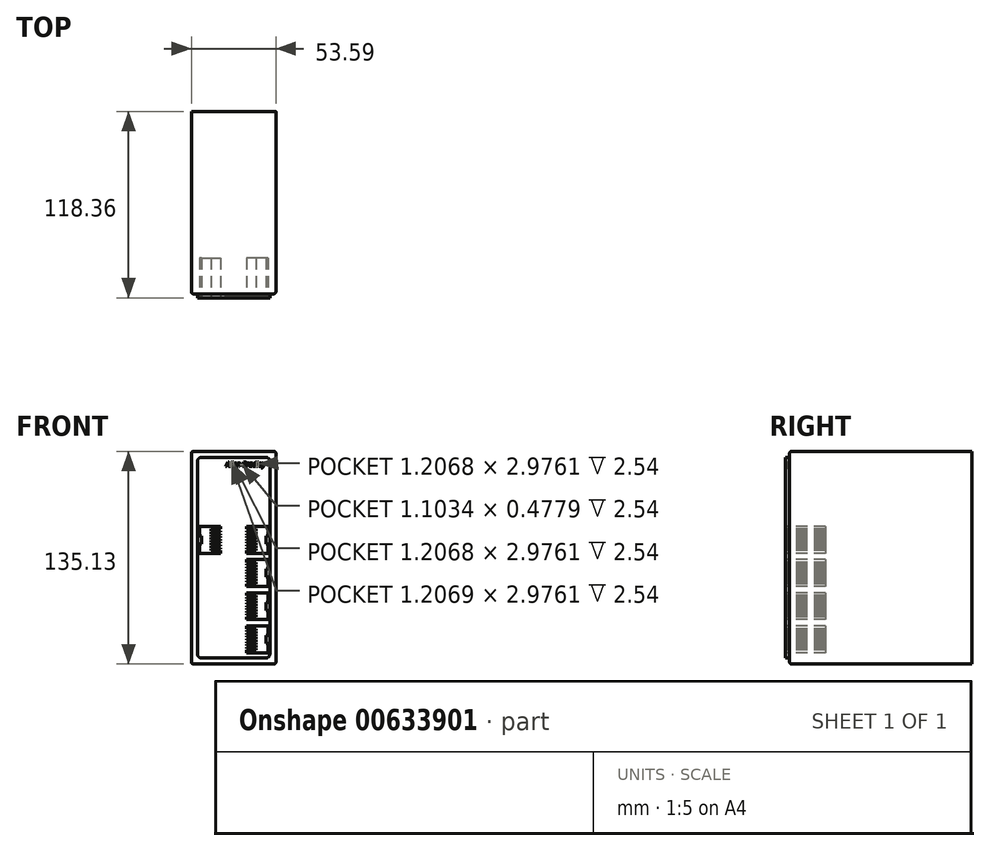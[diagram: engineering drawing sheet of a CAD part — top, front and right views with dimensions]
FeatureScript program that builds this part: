
annotation { "Feature Type Name" : "Feature", "Feature Type Description" : "" }
export const myFeature = defineFeature(function(context is Context, id is Id, definition is map)
    precondition{}
    {
        {
            var Q0;
            Q0=qCreatedBy(makeId("Front.planeOp"),FACE);
            var sketch = newSketch(context, id + "F0", { "sketchPlane" : qUnion([Q0])});
            skLineSegment(sketch, "E0.bottom", {"start": v(0, 0) * mm, "end": v(53.6, 0) * mm});
            skLineSegment(sketch, "E0.top", {"start": v(0, 135.13) * mm, "end": v(53.6, 135.13) * mm});
            skLineSegment(sketch, "E0.left", {"start": v(0, 0) * mm, "end": v(0, 135.13) * mm});
            skLineSegment(sketch, "E0.right", {"start": v(53.6, 0) * mm, "end": v(53.6, 135.13) * mm});
            skSolve(sketch);
        }
        {
            var Q0;
            Q0=makeQuery(id+"F0.imprint","IMPRINT",FACE,{"disambiguationData":[TD([[makeQuery(id+"F0.imprint","IMPRINT",EDGE,{"derivedFrom":sQuery(id+"F0.wireOp",EDGE,"E0.bottom")}),1.0]])]});
            extrude(context, id + "F1", {"entities" : qUnion([Q0]), "depth" : 115.82 * mm, "offsetDistance" : 25.4 * mm});
        }
        {
            var Q0;
            Q0=makeQuery(id+"F1.opExtrude","CAP_FACE",FACE,{"disambiguationData":[OSD([sQuery(id+"F0.wireOp",EDGE,"E0.bottom"),sQuery(id+"F0.wireOp",EDGE,"E0.top"),sQuery(id+"F0.wireOp",EDGE,"E0.left"),sQuery(id+"F0.wireOp",EDGE,"E0.right")])],"isStart":false});
            var sketch = newSketch(context, id + "F2", { "sketchPlane" : qUnion([Q0])});
            skLineSegment(sketch, "E1.0", {"start": v(6.35, 131.32) * mm, "end": v(47.24, 131.32) * mm});
            skLineSegment(sketch, "E1.1", {"start": v(3.81, 6.35) * mm, "end": v(3.81, 128.78) * mm});
            skLineSegment(sketch, "E1.2", {"start": v(6.35, 3.81) * mm, "end": v(47.24, 3.81) * mm});
            skLineSegment(sketch, "E1.3", {"start": v(49.78, 6.35) * mm, "end": v(49.78, 128.78) * mm});
            skPoint(sketch, "E2.visualSharp", {"position": v(3.81, 131.32) * mm});
            skArc(sketch, "E2.filletArc", {"start": v(6.35, 131.32) * mm, "mid": v(4.55, 130.57) * mm, "end": v(3.81, 128.78) * mm});
            skPoint(sketch, "E3.visualSharp", {"position": v(49.78, 131.32) * mm});
            skArc(sketch, "E3.filletArc", {"start": v(49.78, 128.78) * mm, "mid": v(49.04, 130.57) * mm, "end": v(47.24, 131.32) * mm});
            skPoint(sketch, "E4.visualSharp", {"position": v(49.78, 3.81) * mm});
            skArc(sketch, "E4.filletArc", {"start": v(47.24, 3.81) * mm, "mid": v(49.04, 4.55) * mm, "end": v(49.78, 6.35) * mm});
            skPoint(sketch, "E5.visualSharp", {"position": v(3.81, 3.81) * mm});
            skArc(sketch, "E5.filletArc", {"start": v(3.81, 6.35) * mm, "mid": v(4.55, 4.55) * mm, "end": v(6.35, 3.81) * mm});
            skText(sketch, "E6", { "text": "Allen-Bradley", "fontName": "OpenSans-BoldItalic.ttf"});
            const initialGuessF2  = {"E6": [0.02189, 0.12554, 1, 0, 0.00282]};
            skSetInitialGuess(sketch, initialGuessF2);
            skSolve(sketch);
        }
        {
            var Q0;
            Q0 = qSketchRegion(id + "F2", true);
            extrude(context, id + "F3", {"entities" : qUnion([Q0]), "operationType" : NewBodyOperationType.ADD, "depth" : 2.54 * mm, "offsetDistance" : 25.4 * mm});
        }
        {
            var Q0;
            Q0=makeQuery(id+"F1.opExtrude","SWEPT_EDGE",EDGE,{"disambiguationData":[OSD([sQuery(id+"F0.wireOp",EDGE,"E0.top"),sQuery(id+"F0.wireOp",EDGE,"E0.right")])]});
            var Q1;
            Q1=makeQuery(id+"F1.opExtrude","SWEPT_EDGE",EDGE,{"disambiguationData":[OSD([sQuery(id+"F0.wireOp",EDGE,"E0.top"),sQuery(id+"F0.wireOp",EDGE,"E0.left")])]});
            var Q2;
            Q2=makeQuery(id+"F1.opExtrude","CAP_EDGE",EDGE,{"disambiguationData":[OSD([sQuery(id+"F0.wireOp",EDGE,"E0.right")])],"isStart":false});
            var Q3;
            Q3=makeQuery(id+"F1.opExtrude","SWEPT_EDGE",EDGE,{"disambiguationData":[OSD([sQuery(id+"F0.wireOp",EDGE,"E0.bottom"),sQuery(id+"F0.wireOp",EDGE,"E0.right")])]});
            var Q4;
            Q4=makeQuery(id+"F1.opExtrude","CAP_EDGE",EDGE,{"disambiguationData":[OSD([sQuery(id+"F0.wireOp",EDGE,"E0.left")])],"isStart":false});
            var Q5;
            Q5=makeQuery(id+"F1.opExtrude","CAP_EDGE",EDGE,{"disambiguationData":[OSD([sQuery(id+"F0.wireOp",EDGE,"E0.top")])],"isStart":false});
            var Q6;
            Q6=makeQuery(id+"F1.opExtrude","CAP_EDGE",EDGE,{"disambiguationData":[OSD([sQuery(id+"F0.wireOp",EDGE,"E0.bottom")])],"isStart":false});
            var Q7;
            Q7=makeQuery(id+"F1.opExtrude","SWEPT_EDGE",EDGE,{"disambiguationData":[OSD([sQuery(id+"F0.wireOp",EDGE,"E0.bottom"),sQuery(id+"F0.wireOp",EDGE,"E0.left")])]});
            fillet(context, id + "F4", {"entities" : qUnion([Q0, Q1, Q2, Q3, Q4, Q5, Q6, Q7]), "radius" : 1.27 * mm, "tangentPropagation" : true, "allowEdgeOverflow" : false});
        }
        {
            var Q0;
            Q0=makeQuery(id+"F3.opExtrude","CAP_FACE",FACE,{"disambiguationData":[OSD([sQuery(id+"F2.wireOp",EDGE,"E1.0"),sQuery(id+"F2.wireOp",EDGE,"E1.1"),sQuery(id+"F2.wireOp",EDGE,"E1.2"),sQuery(id+"F2.wireOp",EDGE,"E1.3"),sQuery(id+"F2.wireOp",EDGE,"E2.filletArc"),sQuery(id+"F2.wireOp",EDGE,"E3.filletArc"),sQuery(id+"F2.wireOp",EDGE,"E4.filletArc"),sQuery(id+"F2.wireOp",EDGE,"E5.filletArc"),sQuery(id+"F2.wireOp",EDGE,"E6.sketch_text.stroke-0"),sQuery(id+"F2.wireOp",EDGE,"E6.sketch_text.stroke-1"),sQuery(id+"F2.wireOp",EDGE,"E6.sketch_text.stroke-2"),sQuery(id+"F2.wireOp",EDGE,"E6.sketch_text.stroke-3"),sQuery(id+"F2.wireOp",EDGE,"E6.sketch_text.stroke-4"),sQuery(id+"F2.wireOp",EDGE,"E6.sketch_text.stroke-5"),sQuery(id+"F2.wireOp",EDGE,"E6.sketch_text.stroke-6"),sQuery(id+"F2.wireOp",EDGE,"E6.sketch_text.stroke-7"),sQuery(id+"F2.wireOp",EDGE,"E6.sketch_text.stroke-14"),sQuery(id+"F2.wireOp",EDGE,"E6.sketch_text.stroke-15"),sQuery(id+"F2.wireOp",EDGE,"E6.sketch_text.stroke-16"),sQuery(id+"F2.wireOp",EDGE,"E6.sketch_text.stroke-17"),sQuery(id+"F2.wireOp",EDGE,"E6.sketch_text.stroke-18"),sQuery(id+"F2.wireOp",EDGE,"E6.sketch_text.stroke-19"),sQuery(id+"F2.wireOp",EDGE,"E6.sketch_text.stroke-20"),sQuery(id+"F2.wireOp",EDGE,"E6.sketch_text.stroke-21"),sQuery(id+"F2.wireOp",EDGE,"E6.sketch_text.stroke-28"),sQuery(id+"F2.wireOp",EDGE,"E6.sketch_text.stroke-29"),sQuery(id+"F2.wireOp",EDGE,"E6.sketch_text.stroke-30"),sQuery(id+"F2.wireOp",EDGE,"E6.sketch_text.stroke-31"),sQuery(id+"F2.wireOp",EDGE,"E6.sketch_text.stroke-32"),sQuery(id+"F2.wireOp",EDGE,"E6.sketch_text.stroke-33"),sQuery(id+"F2.wireOp",EDGE,"E6.sketch_text.stroke-34"),sQuery(id+"F2.wireOp",EDGE,"E6.sketch_text.stroke-35"),sQuery(id+"F2.wireOp",EDGE,"E6.sketch_text.stroke-36"),sQuery(id+"F2.wireOp",EDGE,"E6.sketch_text.stroke-37"),sQuery(id+"F2.wireOp",EDGE,"E6.sketch_text.stroke-38"),sQuery(id+"F2.wireOp",EDGE,"E6.sketch_text.stroke-39"),sQuery(id+"F2.wireOp",EDGE,"E6.sketch_text.stroke-40"),sQuery(id+"F2.wireOp",EDGE,"E6.sketch_text.stroke-41"),sQuery(id+"F2.wireOp",EDGE,"E6.sketch_text.stroke-42"),sQuery(id+"F2.wireOp",EDGE,"E6.sketch_text.stroke-43"),sQuery(id+"F2.wireOp",EDGE,"E6.sketch_text.stroke-44"),sQuery(id+"F2.wireOp",EDGE,"E6.sketch_text.stroke-45"),sQuery(id+"F2.wireOp",EDGE,"E6.sketch_text.stroke-46"),sQuery(id+"F2.wireOp",EDGE,"E6.sketch_text.stroke-47"),sQuery(id+"F2.wireOp",EDGE,"E6.sketch_text.stroke-48"),sQuery(id+"F2.wireOp",EDGE,"E6.sketch_text.stroke-49"),sQuery(id+"F2.wireOp",EDGE,"E6.sketch_text.stroke-50"),sQuery(id+"F2.wireOp",EDGE,"E6.sketch_text.stroke-51"),sQuery(id+"F2.wireOp",EDGE,"E6.sketch_text.stroke-52"),sQuery(id+"F2.wireOp",EDGE,"E6.sketch_text.stroke-53"),sQuery(id+"F2.wireOp",EDGE,"E6.sketch_text.stroke-54"),sQuery(id+"F2.wireOp",EDGE,"E6.sketch_text.stroke-55"),sQuery(id+"F2.wireOp",EDGE,"E6.sketch_text.stroke-56"),sQuery(id+"F2.wireOp",EDGE,"E6.sketch_text.stroke-57"),sQuery(id+"F2.wireOp",EDGE,"E6.sketch_text.stroke-58"),sQuery(id+"F2.wireOp",EDGE,"E6.sketch_text.stroke-59"),sQuery(id+"F2.wireOp",EDGE,"E6.sketch_text.stroke-60"),sQuery(id+"F2.wireOp",EDGE,"E6.sketch_text.stroke-61"),sQuery(id+"F2.wireOp",EDGE,"E6.sketch_text.stroke-62"),sQuery(id+"F2.wireOp",EDGE,"E6.sketch_text.stroke-63"),sQuery(id+"F2.wireOp",EDGE,"E6.sketch_text.stroke-64"),sQuery(id+"F2.wireOp",EDGE,"E6.sketch_text.stroke-65"),sQuery(id+"F2.wireOp",EDGE,"E6.sketch_text.stroke-66"),sQuery(id+"F2.wireOp",EDGE,"E6.sketch_text.stroke-67"),sQuery(id+"F2.wireOp",EDGE,"E6.sketch_text.stroke-68"),sQuery(id+"F2.wireOp",EDGE,"E6.sketch_text.stroke-69"),sQuery(id+"F2.wireOp",EDGE,"E6.sketch_text.stroke-70"),sQuery(id+"F2.wireOp",EDGE,"E6.sketch_text.stroke-71"),sQuery(id+"F2.wireOp",EDGE,"E6.sketch_text.stroke-72"),sQuery(id+"F2.wireOp",EDGE,"E6.sketch_text.stroke-73"),sQuery(id+"F2.wireOp",EDGE,"E6.sketch_text.stroke-74"),sQuery(id+"F2.wireOp",EDGE,"E6.sketch_text.stroke-75"),sQuery(id+"F2.wireOp",EDGE,"E6.sketch_text.stroke-76"),sQuery(id+"F2.wireOp",EDGE,"E6.sketch_text.stroke-77"),sQuery(id+"F2.wireOp",EDGE,"E6.sketch_text.stroke-78"),sQuery(id+"F2.wireOp",EDGE,"E6.sketch_text.stroke-91"),sQuery(id+"F2.wireOp",EDGE,"E6.sketch_text.stroke-92"),sQuery(id+"F2.wireOp",EDGE,"E6.sketch_text.stroke-93"),sQuery(id+"F2.wireOp",EDGE,"E6.sketch_text.stroke-94"),sQuery(id+"F2.wireOp",EDGE,"E6.sketch_text.stroke-95"),sQuery(id+"F2.wireOp",EDGE,"E6.sketch_text.stroke-96"),sQuery(id+"F2.wireOp",EDGE,"E6.sketch_text.stroke-97"),sQuery(id+"F2.wireOp",EDGE,"E6.sketch_text.stroke-98"),sQuery(id+"F2.wireOp",EDGE,"E6.sketch_text.stroke-99"),sQuery(id+"F2.wireOp",EDGE,"E6.sketch_text.stroke-100"),sQuery(id+"F2.wireOp",EDGE,"E6.sketch_text.stroke-101"),sQuery(id+"F2.wireOp",EDGE,"E6.sketch_text.stroke-102"),sQuery(id+"F2.wireOp",EDGE,"E6.sketch_text.stroke-103"),sQuery(id+"F2.wireOp",EDGE,"E6.sketch_text.stroke-104"),sQuery(id+"F2.wireOp",EDGE,"E6.sketch_text.stroke-105"),sQuery(id+"F2.wireOp",EDGE,"E6.sketch_text.stroke-106"),sQuery(id+"F2.wireOp",EDGE,"E6.sketch_text.stroke-107"),sQuery(id+"F2.wireOp",EDGE,"E6.sketch_text.stroke-108"),sQuery(id+"F2.wireOp",EDGE,"E6.sketch_text.stroke-109"),sQuery(id+"F2.wireOp",EDGE,"E6.sketch_text.stroke-110"),sQuery(id+"F2.wireOp",EDGE,"E6.sketch_text.stroke-111"),sQuery(id+"F2.wireOp",EDGE,"E6.sketch_text.stroke-112"),sQuery(id+"F2.wireOp",EDGE,"E6.sketch_text.stroke-113"),sQuery(id+"F2.wireOp",EDGE,"E6.sketch_text.stroke-114"),sQuery(id+"F2.wireOp",EDGE,"E6.sketch_text.stroke-115"),sQuery(id+"F2.wireOp",EDGE,"E6.sketch_text.stroke-116"),sQuery(id+"F2.wireOp",EDGE,"E6.sketch_text.stroke-117"),sQuery(id+"F2.wireOp",EDGE,"E6.sketch_text.stroke-128"),sQuery(id+"F2.wireOp",EDGE,"E6.sketch_text.stroke-129"),sQuery(id+"F2.wireOp",EDGE,"E6.sketch_text.stroke-130"),sQuery(id+"F2.wireOp",EDGE,"E6.sketch_text.stroke-131"),sQuery(id+"F2.wireOp",EDGE,"E6.sketch_text.stroke-132"),sQuery(id+"F2.wireOp",EDGE,"E6.sketch_text.stroke-133"),sQuery(id+"F2.wireOp",EDGE,"E6.sketch_text.stroke-134"),sQuery(id+"F2.wireOp",EDGE,"E6.sketch_text.stroke-135"),sQuery(id+"F2.wireOp",EDGE,"E6.sketch_text.stroke-136"),sQuery(id+"F2.wireOp",EDGE,"E6.sketch_text.stroke-137"),sQuery(id+"F2.wireOp",EDGE,"E6.sketch_text.stroke-138"),sQuery(id+"F2.wireOp",EDGE,"E6.sketch_text.stroke-139"),sQuery(id+"F2.wireOp",EDGE,"E6.sketch_text.stroke-140"),sQuery(id+"F2.wireOp",EDGE,"E6.sketch_text.stroke-141"),sQuery(id+"F2.wireOp",EDGE,"E6.sketch_text.stroke-142"),sQuery(id+"F2.wireOp",EDGE,"E6.sketch_text.stroke-143"),sQuery(id+"F2.wireOp",EDGE,"E6.sketch_text.stroke-144"),sQuery(id+"F2.wireOp",EDGE,"E6.sketch_text.stroke-145"),sQuery(id+"F2.wireOp",EDGE,"E6.sketch_text.stroke-155"),sQuery(id+"F2.wireOp",EDGE,"E6.sketch_text.stroke-156"),sQuery(id+"F2.wireOp",EDGE,"E6.sketch_text.stroke-157"),sQuery(id+"F2.wireOp",EDGE,"E6.sketch_text.stroke-158"),sQuery(id+"F2.wireOp",EDGE,"E6.sketch_text.stroke-165"),sQuery(id+"F2.wireOp",EDGE,"E6.sketch_text.stroke-166"),sQuery(id+"F2.wireOp",EDGE,"E6.sketch_text.stroke-167"),sQuery(id+"F2.wireOp",EDGE,"E6.sketch_text.stroke-168"),sQuery(id+"F2.wireOp",EDGE,"E6.sketch_text.stroke-169"),sQuery(id+"F2.wireOp",EDGE,"E6.sketch_text.stroke-170"),sQuery(id+"F2.wireOp",EDGE,"E6.sketch_text.stroke-171"),sQuery(id+"F2.wireOp",EDGE,"E6.sketch_text.stroke-172"),sQuery(id+"F2.wireOp",EDGE,"E6.sketch_text.stroke-173"),sQuery(id+"F2.wireOp",EDGE,"E6.sketch_text.stroke-174"),sQuery(id+"F2.wireOp",EDGE,"E6.sketch_text.stroke-175"),sQuery(id+"F2.wireOp",EDGE,"E6.sketch_text.stroke-176"),sQuery(id+"F2.wireOp",EDGE,"E6.sketch_text.stroke-177"),sQuery(id+"F2.wireOp",EDGE,"E6.sketch_text.stroke-178"),sQuery(id+"F2.wireOp",EDGE,"E6.sketch_text.stroke-179"),sQuery(id+"F2.wireOp",EDGE,"E6.sketch_text.stroke-180"),sQuery(id+"F2.wireOp",EDGE,"E6.sketch_text.stroke-181"),sQuery(id+"F2.wireOp",EDGE,"E6.sketch_text.stroke-182"),sQuery(id+"F2.wireOp",EDGE,"E6.sketch_text.stroke-183"),sQuery(id+"F2.wireOp",EDGE,"E6.sketch_text.stroke-184"),sQuery(id+"F2.wireOp",EDGE,"E6.sketch_text.stroke-185"),sQuery(id+"F2.wireOp",EDGE,"E6.sketch_text.stroke-186"),sQuery(id+"F2.wireOp",EDGE,"E6.sketch_text.stroke-187"),sQuery(id+"F2.wireOp",EDGE,"E6.sketch_text.stroke-188"),sQuery(id+"F2.wireOp",EDGE,"E6.sketch_text.stroke-189"),sQuery(id+"F2.wireOp",EDGE,"E6.sketch_text.stroke-190"),sQuery(id+"F2.wireOp",EDGE,"E6.sketch_text.stroke-191"),sQuery(id+"F2.wireOp",EDGE,"E6.sketch_text.stroke-192"),sQuery(id+"F2.wireOp",EDGE,"E6.sketch_text.stroke-193"),sQuery(id+"F2.wireOp",EDGE,"E6.sketch_text.stroke-194"),sQuery(id+"F2.wireOp",EDGE,"E6.sketch_text.stroke-195"),sQuery(id+"F2.wireOp",EDGE,"E6.sketch_text.stroke-196"),sQuery(id+"F2.wireOp",EDGE,"E6.sketch_text.stroke-197"),sQuery(id+"F2.wireOp",EDGE,"E6.sketch_text.stroke-198"),sQuery(id+"F2.wireOp",EDGE,"E6.sketch_text.stroke-199")])],"isStart":false});
            var sketch = newSketch(context, id + "F5", { "sketchPlane" : qUnion([Q0])});
            skLineSegment(sketch, "E7.top", {"start": v(5.08, 70.39) * mm, "end": v(18.55, 70.39) * mm});
            skLineSegment(sketch, "E7.left", {"start": v(5.08, 87.4) * mm, "end": v(5.08, 70.39) * mm});
            skLineSegment(sketch, "E7.right", {"start": v(18.55, 87.4) * mm, "end": v(18.55, 70.39) * mm});
            skLineSegment(sketch, "E8", {"start": v(6.35, 78.9) * mm, "end": v(6.35, 81.44) * mm});
            skLineSegment(sketch, "E9", {"start": v(6.35, 81.44) * mm, "end": v(5.08, 81.44) * mm});
            skLineSegment(sketch, "E10.MirrorCS", {"start": v(6.35, 76.36) * mm, "end": v(5.08, 76.36) * mm});
            skLineSegment(sketch, "E11.MirrorCS", {"start": v(6.35, 78.9) * mm, "end": v(6.35, 76.36) * mm});
            skLineSegment(sketch, "E12.bottom", {"start": v(12.48, 73.23) * mm, "end": v(18.56, 73.23) * mm});
            skLineSegment(sketch, "E12.top", {"start": v(12.48, 72.09) * mm, "end": v(18.56, 72.09) * mm});
            skLineSegment(sketch, "E12.left", {"start": v(12.48, 73.23) * mm, "end": v(12.48, 72.09) * mm});
            skLineSegment(sketch, "E12.right", {"start": v(18.56, 73.23) * mm, "end": v(18.56, 72.09) * mm});
            skLineSegment(sketch, "E13.0.1.0", {"start": v(18.56, 75.01) * mm, "end": v(18.56, 73.86) * mm});
            skLineSegment(sketch, "E13.0.1.1", {"start": v(12.48, 75.01) * mm, "end": v(12.48, 73.86) * mm});
            skLineSegment(sketch, "E13.0.1.2", {"start": v(12.48, 75.01) * mm, "end": v(18.56, 75.01) * mm});
            skLineSegment(sketch, "E13.0.1.3", {"start": v(12.48, 73.86) * mm, "end": v(18.56, 73.86) * mm});
            skLineSegment(sketch, "E13.0.2.0", {"start": v(18.56, 76.79) * mm, "end": v(18.56, 75.64) * mm});
            skLineSegment(sketch, "E13.0.2.1", {"start": v(12.48, 76.79) * mm, "end": v(12.48, 75.64) * mm});
            skLineSegment(sketch, "E13.0.2.2", {"start": v(12.48, 76.79) * mm, "end": v(18.56, 76.79) * mm});
            skLineSegment(sketch, "E13.0.2.3", {"start": v(12.48, 75.64) * mm, "end": v(18.56, 75.64) * mm});
            skLineSegment(sketch, "E13.0.3.0", {"start": v(18.56, 78.57) * mm, "end": v(18.56, 77.42) * mm});
            skLineSegment(sketch, "E13.0.3.1", {"start": v(12.48, 78.57) * mm, "end": v(12.48, 77.42) * mm});
            skLineSegment(sketch, "E13.0.3.2", {"start": v(12.48, 78.57) * mm, "end": v(18.56, 78.57) * mm});
            skLineSegment(sketch, "E13.0.3.3", {"start": v(12.48, 77.42) * mm, "end": v(18.56, 77.42) * mm});
            skLineSegment(sketch, "E13.0.4.0", {"start": v(18.56, 80.35) * mm, "end": v(18.56, 79.2) * mm});
            skLineSegment(sketch, "E13.0.4.1", {"start": v(12.48, 80.35) * mm, "end": v(12.48, 79.2) * mm});
            skLineSegment(sketch, "E13.0.4.2", {"start": v(12.48, 80.35) * mm, "end": v(18.56, 80.35) * mm});
            skLineSegment(sketch, "E13.0.4.3", {"start": v(12.48, 79.2) * mm, "end": v(18.56, 79.2) * mm});
            skLineSegment(sketch, "E13.0.5.0", {"start": v(18.56, 82.12) * mm, "end": v(18.56, 80.98) * mm});
            skLineSegment(sketch, "E13.0.5.1", {"start": v(12.48, 82.12) * mm, "end": v(12.48, 80.98) * mm});
            skLineSegment(sketch, "E13.0.5.2", {"start": v(12.48, 82.12) * mm, "end": v(18.56, 82.12) * mm});
            skLineSegment(sketch, "E13.0.5.3", {"start": v(12.48, 80.98) * mm, "end": v(18.56, 80.98) * mm});
            skLineSegment(sketch, "E13.0.6.0", {"start": v(18.56, 83.9) * mm, "end": v(18.56, 82.75) * mm});
            skLineSegment(sketch, "E13.0.6.1", {"start": v(12.48, 83.9) * mm, "end": v(12.48, 82.75) * mm});
            skLineSegment(sketch, "E13.0.6.2", {"start": v(12.48, 83.9) * mm, "end": v(18.56, 83.9) * mm});
            skLineSegment(sketch, "E13.0.6.3", {"start": v(12.48, 82.75) * mm, "end": v(18.56, 82.75) * mm});
            skLineSegment(sketch, "E13.0.7.0", {"start": v(18.56, 85.68) * mm, "end": v(18.56, 84.53) * mm});
            skLineSegment(sketch, "E13.0.7.1", {"start": v(12.48, 85.68) * mm, "end": v(12.48, 84.53) * mm});
            skLineSegment(sketch, "E13.0.7.2", {"start": v(12.48, 85.68) * mm, "end": v(18.56, 85.68) * mm});
            skLineSegment(sketch, "E13.0.7.3", {"start": v(12.48, 84.53) * mm, "end": v(18.56, 84.53) * mm});
            skLineSegment(sketch, "E13.direction1", {"start": v(10.05, 84.5) * mm, "end": v(10.05, 84.5) * mm});
            skLineSegment(sketch, "E13.direction2", {"start": v(12.48, 72.09) * mm, "end": v(12.48, 73.86) * mm, "construction": true});
            skLineSegment(sketch, "E14", {"start": v(18.56, 78.57) * mm, "end": v(18.56, 79.2) * mm});
            skLineSegment(sketch, "E15.0.1.0", {"start": v(12.48, 54.56) * mm, "end": v(18.56, 54.56) * mm});
            skLineSegment(sketch, "E15.0.1.1", {"start": v(12.48, 52.15) * mm, "end": v(18.56, 52.15) * mm});
            skLineSegment(sketch, "E15.0.1.2", {"start": v(12.48, 62.82) * mm, "end": v(18.56, 62.82) * mm});
            skLineSegment(sketch, "E15.0.1.3", {"start": v(12.48, 63.45) * mm, "end": v(18.56, 63.45) * mm});
            skLineSegment(sketch, "E15.0.1.4", {"start": v(12.48, 56.34) * mm, "end": v(18.56, 56.34) * mm});
            skLineSegment(sketch, "E15.0.1.5", {"start": v(12.48, 59.9) * mm, "end": v(18.56, 59.9) * mm});
            skLineSegment(sketch, "E15.0.1.6", {"start": v(12.48, 61.67) * mm, "end": v(18.56, 61.67) * mm});
            skLineSegment(sketch, "E15.0.1.7", {"start": v(12.48, 51) * mm, "end": v(18.56, 51) * mm});
            skLineSegment(sketch, "E15.0.1.8", {"start": v(12.48, 55.7) * mm, "end": v(18.56, 55.7) * mm});
            skLineSegment(sketch, "E15.0.1.9", {"start": v(12.48, 59.26) * mm, "end": v(18.56, 59.26) * mm});
            skLineSegment(sketch, "E15.0.1.10", {"start": v(12.48, 52.78) * mm, "end": v(18.56, 52.78) * mm});
            skLineSegment(sketch, "E15.0.1.11", {"start": v(12.48, 57.49) * mm, "end": v(18.56, 57.49) * mm});
            skLineSegment(sketch, "E15.0.1.12", {"start": v(12.48, 61.04) * mm, "end": v(18.56, 61.04) * mm});
            skLineSegment(sketch, "E15.0.1.13", {"start": v(12.48, 64.6) * mm, "end": v(18.56, 64.6) * mm});
            skLineSegment(sketch, "E15.0.1.14", {"start": v(12.48, 58.12) * mm, "end": v(18.56, 58.12) * mm});
            skLineSegment(sketch, "E15.0.1.15", {"start": v(5.08, 66.32) * mm, "end": v(18.55, 66.32) * mm});
            skLineSegment(sketch, "E15.0.1.16", {"start": v(5.08, 49.3) * mm, "end": v(18.55, 49.3) * mm});
            skLineSegment(sketch, "E15.0.1.17", {"start": v(5.08, 66.32) * mm, "end": v(5.08, 49.3) * mm});
            skLineSegment(sketch, "E15.0.1.18", {"start": v(12.48, 53.93) * mm, "end": v(18.56, 53.93) * mm});
            skLineSegment(sketch, "E15.0.1.19", {"start": v(6.35, 57.82) * mm, "end": v(6.35, 60.36) * mm});
            skLineSegment(sketch, "E15.0.1.20", {"start": v(6.35, 55.28) * mm, "end": v(5.08, 55.28) * mm});
            skLineSegment(sketch, "E15.0.1.21", {"start": v(6.35, 60.36) * mm, "end": v(5.08, 60.36) * mm});
            skLineSegment(sketch, "E15.0.1.22", {"start": v(6.35, 57.82) * mm, "end": v(6.35, 55.28) * mm});
            skLineSegment(sketch, "E15.0.1.23", {"start": v(12.48, 64.6) * mm, "end": v(12.48, 63.45) * mm});
            skLineSegment(sketch, "E15.0.1.24", {"start": v(18.55, 66.32) * mm, "end": v(18.55, 49.3) * mm});
            skLineSegment(sketch, "E15.0.1.25", {"start": v(18.56, 64.6) * mm, "end": v(18.56, 63.45) * mm});
            skLineSegment(sketch, "E15.0.1.26", {"start": v(18.56, 62.82) * mm, "end": v(18.56, 61.67) * mm});
            skLineSegment(sketch, "E15.0.1.27", {"start": v(12.48, 52.15) * mm, "end": v(12.48, 51) * mm});
            skLineSegment(sketch, "E15.0.1.28", {"start": v(18.56, 61.04) * mm, "end": v(18.56, 59.9) * mm});
            skLineSegment(sketch, "E15.0.1.29", {"start": v(12.48, 53.93) * mm, "end": v(12.48, 52.78) * mm});
            skLineSegment(sketch, "E15.0.1.30", {"start": v(18.56, 55.7) * mm, "end": v(18.56, 54.56) * mm});
            skLineSegment(sketch, "E15.0.1.31", {"start": v(12.48, 51) * mm, "end": v(12.48, 52.78) * mm, "construction": true});
            skLineSegment(sketch, "E15.0.1.32", {"start": v(12.48, 62.82) * mm, "end": v(12.48, 61.67) * mm});
            skLineSegment(sketch, "E15.0.1.33", {"start": v(18.56, 52.15) * mm, "end": v(18.56, 51) * mm});
            skLineSegment(sketch, "E15.0.1.34", {"start": v(18.56, 53.93) * mm, "end": v(18.56, 52.78) * mm});
            skLineSegment(sketch, "E15.0.1.35", {"start": v(12.48, 61.04) * mm, "end": v(12.48, 59.9) * mm});
            skLineSegment(sketch, "E15.0.1.36", {"start": v(18.56, 57.49) * mm, "end": v(18.56, 58.12) * mm});
            skLineSegment(sketch, "E15.0.1.37", {"start": v(12.48, 55.7) * mm, "end": v(12.48, 54.56) * mm});
            skLineSegment(sketch, "E15.0.1.38", {"start": v(18.56, 57.49) * mm, "end": v(18.56, 56.34) * mm});
            skLineSegment(sketch, "E15.0.1.39", {"start": v(18.56, 59.26) * mm, "end": v(18.56, 58.12) * mm});
            skLineSegment(sketch, "E15.0.1.40", {"start": v(12.48, 59.26) * mm, "end": v(12.48, 58.12) * mm});
            skLineSegment(sketch, "E15.0.1.41", {"start": v(12.48, 57.49) * mm, "end": v(12.48, 56.34) * mm});
            skLineSegment(sketch, "E15.0.2.0", {"start": v(12.48, 33.48) * mm, "end": v(18.56, 33.48) * mm});
            skLineSegment(sketch, "E15.0.2.1", {"start": v(12.48, 31.07) * mm, "end": v(18.56, 31.07) * mm});
            skLineSegment(sketch, "E15.0.2.2", {"start": v(12.48, 41.74) * mm, "end": v(18.56, 41.74) * mm});
            skLineSegment(sketch, "E15.0.2.3", {"start": v(12.48, 42.37) * mm, "end": v(18.56, 42.37) * mm});
            skLineSegment(sketch, "E15.0.2.4", {"start": v(12.48, 35.26) * mm, "end": v(18.56, 35.26) * mm});
            skLineSegment(sketch, "E15.0.2.5", {"start": v(12.48, 38.81) * mm, "end": v(18.56, 38.81) * mm});
            skLineSegment(sketch, "E15.0.2.6", {"start": v(12.48, 40.59) * mm, "end": v(18.56, 40.59) * mm});
            skLineSegment(sketch, "E15.0.2.7", {"start": v(12.48, 29.92) * mm, "end": v(18.56, 29.92) * mm});
            skLineSegment(sketch, "E15.0.2.8", {"start": v(12.48, 34.63) * mm, "end": v(18.56, 34.63) * mm});
            skLineSegment(sketch, "E15.0.2.9", {"start": v(12.48, 38.18) * mm, "end": v(18.56, 38.18) * mm});
            skLineSegment(sketch, "E15.0.2.10", {"start": v(12.48, 31.7) * mm, "end": v(18.56, 31.7) * mm});
            skLineSegment(sketch, "E15.0.2.11", {"start": v(12.48, 36.4) * mm, "end": v(18.56, 36.4) * mm});
            skLineSegment(sketch, "E15.0.2.12", {"start": v(12.48, 39.96) * mm, "end": v(18.56, 39.96) * mm});
            skLineSegment(sketch, "E15.0.2.13", {"start": v(12.48, 43.52) * mm, "end": v(18.56, 43.52) * mm});
            skLineSegment(sketch, "E15.0.2.14", {"start": v(12.48, 37.03) * mm, "end": v(18.56, 37.03) * mm});
            skLineSegment(sketch, "E15.0.2.15", {"start": v(5.08, 45.24) * mm, "end": v(18.55, 45.24) * mm});
            skLineSegment(sketch, "E15.0.2.16", {"start": v(5.08, 28.23) * mm, "end": v(18.55, 28.23) * mm});
            skLineSegment(sketch, "E15.0.2.17", {"start": v(5.08, 45.24) * mm, "end": v(5.08, 28.23) * mm});
            skLineSegment(sketch, "E15.0.2.18", {"start": v(12.48, 32.85) * mm, "end": v(18.56, 32.85) * mm});
            skLineSegment(sketch, "E15.0.2.19", {"start": v(6.35, 36.73) * mm, "end": v(6.35, 39.27) * mm});
            skLineSegment(sketch, "E15.0.2.20", {"start": v(6.35, 34.2) * mm, "end": v(5.08, 34.2) * mm});
            skLineSegment(sketch, "E15.0.2.21", {"start": v(6.35, 39.27) * mm, "end": v(5.08, 39.27) * mm});
            skLineSegment(sketch, "E15.0.2.22", {"start": v(6.35, 36.73) * mm, "end": v(6.35, 34.2) * mm});
            skLineSegment(sketch, "E15.0.2.23", {"start": v(12.48, 43.52) * mm, "end": v(12.48, 42.37) * mm});
            skLineSegment(sketch, "E15.0.2.24", {"start": v(18.55, 45.24) * mm, "end": v(18.55, 28.23) * mm});
            skLineSegment(sketch, "E15.0.2.25", {"start": v(18.56, 43.52) * mm, "end": v(18.56, 42.37) * mm});
            skLineSegment(sketch, "E15.0.2.26", {"start": v(18.56, 41.74) * mm, "end": v(18.56, 40.59) * mm});
            skLineSegment(sketch, "E15.0.2.27", {"start": v(12.48, 31.07) * mm, "end": v(12.48, 29.92) * mm});
            skLineSegment(sketch, "E15.0.2.28", {"start": v(18.56, 39.96) * mm, "end": v(18.56, 38.81) * mm});
            skLineSegment(sketch, "E15.0.2.29", {"start": v(12.48, 32.85) * mm, "end": v(12.48, 31.7) * mm});
            skLineSegment(sketch, "E15.0.2.30", {"start": v(18.56, 34.63) * mm, "end": v(18.56, 33.48) * mm});
            skLineSegment(sketch, "E15.0.2.31", {"start": v(12.48, 29.92) * mm, "end": v(12.48, 31.7) * mm, "construction": true});
            skLineSegment(sketch, "E15.0.2.32", {"start": v(12.48, 41.74) * mm, "end": v(12.48, 40.59) * mm});
            skLineSegment(sketch, "E15.0.2.33", {"start": v(18.56, 31.07) * mm, "end": v(18.56, 29.92) * mm});
            skLineSegment(sketch, "E15.0.2.34", {"start": v(18.56, 32.85) * mm, "end": v(18.56, 31.7) * mm});
            skLineSegment(sketch, "E15.0.2.35", {"start": v(12.48, 39.96) * mm, "end": v(12.48, 38.81) * mm});
            skLineSegment(sketch, "E15.0.2.36", {"start": v(18.56, 36.4) * mm, "end": v(18.56, 37.03) * mm});
            skLineSegment(sketch, "E15.0.2.37", {"start": v(12.48, 34.63) * mm, "end": v(12.48, 33.48) * mm});
            skLineSegment(sketch, "E15.0.2.38", {"start": v(18.56, 36.4) * mm, "end": v(18.56, 35.26) * mm});
            skLineSegment(sketch, "E15.0.2.39", {"start": v(18.56, 38.18) * mm, "end": v(18.56, 37.03) * mm});
            skLineSegment(sketch, "E15.0.2.40", {"start": v(12.48, 38.18) * mm, "end": v(12.48, 37.03) * mm});
            skLineSegment(sketch, "E15.0.2.41", {"start": v(12.48, 36.4) * mm, "end": v(12.48, 35.26) * mm});
            skLineSegment(sketch, "E15.0.3.0", {"start": v(12.48, 12.4) * mm, "end": v(18.56, 12.4) * mm});
            skLineSegment(sketch, "E15.0.3.1", {"start": v(12.48, 9.99) * mm, "end": v(18.56, 9.99) * mm});
            skLineSegment(sketch, "E15.0.3.2", {"start": v(12.48, 20.66) * mm, "end": v(18.56, 20.66) * mm});
            skLineSegment(sketch, "E15.0.3.3", {"start": v(12.48, 21.29) * mm, "end": v(18.56, 21.29) * mm});
            skLineSegment(sketch, "E15.0.3.4", {"start": v(12.48, 14.17) * mm, "end": v(18.56, 14.17) * mm});
            skLineSegment(sketch, "E15.0.3.5", {"start": v(12.48, 17.73) * mm, "end": v(18.56, 17.73) * mm});
            skLineSegment(sketch, "E15.0.3.6", {"start": v(12.48, 19.5) * mm, "end": v(18.56, 19.5) * mm});
            skLineSegment(sketch, "E15.0.3.7", {"start": v(12.48, 8.84) * mm, "end": v(18.56, 8.84) * mm});
            skLineSegment(sketch, "E15.0.3.8", {"start": v(12.48, 13.54) * mm, "end": v(18.56, 13.54) * mm});
            skLineSegment(sketch, "E15.0.3.9", {"start": v(12.48, 17.1) * mm, "end": v(18.56, 17.1) * mm});
            skLineSegment(sketch, "E15.0.3.10", {"start": v(12.48, 10.62) * mm, "end": v(18.56, 10.62) * mm});
            skLineSegment(sketch, "E15.0.3.11", {"start": v(12.48, 15.32) * mm, "end": v(18.56, 15.32) * mm});
            skLineSegment(sketch, "E15.0.3.12", {"start": v(12.48, 18.88) * mm, "end": v(18.56, 18.88) * mm});
            skLineSegment(sketch, "E15.0.3.13", {"start": v(12.48, 22.43) * mm, "end": v(18.56, 22.43) * mm});
            skLineSegment(sketch, "E15.0.3.14", {"start": v(12.48, 15.95) * mm, "end": v(18.56, 15.95) * mm});
            skLineSegment(sketch, "E15.0.3.15", {"start": v(5.08, 24.16) * mm, "end": v(18.55, 24.16) * mm});
            skLineSegment(sketch, "E15.0.3.16", {"start": v(5.08, 7.14) * mm, "end": v(18.55, 7.14) * mm});
            skLineSegment(sketch, "E15.0.3.17", {"start": v(5.08, 24.16) * mm, "end": v(5.08, 7.14) * mm});
            skLineSegment(sketch, "E15.0.3.18", {"start": v(12.48, 11.77) * mm, "end": v(18.56, 11.77) * mm});
            skLineSegment(sketch, "E15.0.3.19", {"start": v(6.35, 15.65) * mm, "end": v(6.35, 18.2) * mm});
            skLineSegment(sketch, "E15.0.3.20", {"start": v(6.35, 13.11) * mm, "end": v(5.08, 13.11) * mm});
            skLineSegment(sketch, "E15.0.3.21", {"start": v(6.35, 18.2) * mm, "end": v(5.08, 18.2) * mm});
            skLineSegment(sketch, "E15.0.3.22", {"start": v(6.35, 15.65) * mm, "end": v(6.35, 13.11) * mm});
            skLineSegment(sketch, "E15.0.3.23", {"start": v(12.48, 22.43) * mm, "end": v(12.48, 21.29) * mm});
            skLineSegment(sketch, "E15.0.3.24", {"start": v(18.55, 24.16) * mm, "end": v(18.55, 7.14) * mm});
            skLineSegment(sketch, "E15.0.3.25", {"start": v(18.56, 22.43) * mm, "end": v(18.56, 21.29) * mm});
            skLineSegment(sketch, "E15.0.3.26", {"start": v(18.56, 20.66) * mm, "end": v(18.56, 19.5) * mm});
            skLineSegment(sketch, "E15.0.3.27", {"start": v(12.48, 9.99) * mm, "end": v(12.48, 8.84) * mm});
            skLineSegment(sketch, "E15.0.3.28", {"start": v(18.56, 18.88) * mm, "end": v(18.56, 17.73) * mm});
            skLineSegment(sketch, "E15.0.3.29", {"start": v(12.48, 11.77) * mm, "end": v(12.48, 10.62) * mm});
            skLineSegment(sketch, "E15.0.3.30", {"start": v(18.56, 13.54) * mm, "end": v(18.56, 12.4) * mm});
            skLineSegment(sketch, "E15.0.3.31", {"start": v(12.48, 8.84) * mm, "end": v(12.48, 10.62) * mm, "construction": true});
            skLineSegment(sketch, "E15.0.3.32", {"start": v(12.48, 20.66) * mm, "end": v(12.48, 19.5) * mm});
            skLineSegment(sketch, "E15.0.3.33", {"start": v(18.56, 9.99) * mm, "end": v(18.56, 8.84) * mm});
            skLineSegment(sketch, "E15.0.3.34", {"start": v(18.56, 11.77) * mm, "end": v(18.56, 10.62) * mm});
            skLineSegment(sketch, "E15.0.3.35", {"start": v(12.48, 18.88) * mm, "end": v(12.48, 17.73) * mm});
            skLineSegment(sketch, "E15.0.3.36", {"start": v(18.56, 15.32) * mm, "end": v(18.56, 15.95) * mm});
            skLineSegment(sketch, "E15.0.3.37", {"start": v(12.48, 13.54) * mm, "end": v(12.48, 12.4) * mm});
            skLineSegment(sketch, "E15.0.3.38", {"start": v(18.56, 15.32) * mm, "end": v(18.56, 14.17) * mm});
            skLineSegment(sketch, "E15.0.3.39", {"start": v(18.56, 17.1) * mm, "end": v(18.56, 15.95) * mm});
            skLineSegment(sketch, "E15.0.3.40", {"start": v(12.48, 17.1) * mm, "end": v(12.48, 15.95) * mm});
            skLineSegment(sketch, "E15.0.3.41", {"start": v(12.48, 15.32) * mm, "end": v(12.48, 14.17) * mm});
            skLineSegment(sketch, "E15.1.0.15", {"start": v(5.08, 87.4) * mm, "end": v(18.55, 87.4) * mm});
            skLineSegment(sketch, "E15.1.1.0", {"start": v(12.48, 54.56) * mm, "end": v(18.56, 54.56) * mm});
            skLineSegment(sketch, "E15.1.1.1", {"start": v(12.48, 52.15) * mm, "end": v(18.56, 52.15) * mm});
            skLineSegment(sketch, "E15.1.1.2", {"start": v(12.48, 62.82) * mm, "end": v(18.56, 62.82) * mm});
            skLineSegment(sketch, "E15.1.1.3", {"start": v(12.48, 63.45) * mm, "end": v(18.56, 63.45) * mm});
            skLineSegment(sketch, "E15.1.1.4", {"start": v(12.48, 56.34) * mm, "end": v(18.56, 56.34) * mm});
            skLineSegment(sketch, "E15.1.1.5", {"start": v(12.48, 59.9) * mm, "end": v(18.56, 59.9) * mm});
            skLineSegment(sketch, "E15.1.1.6", {"start": v(12.48, 61.67) * mm, "end": v(18.56, 61.67) * mm});
            skLineSegment(sketch, "E15.1.1.7", {"start": v(12.48, 51) * mm, "end": v(18.56, 51) * mm});
            skLineSegment(sketch, "E15.1.1.8", {"start": v(12.48, 55.7) * mm, "end": v(18.56, 55.7) * mm});
            skLineSegment(sketch, "E15.1.1.9", {"start": v(12.48, 59.26) * mm, "end": v(18.56, 59.26) * mm});
            skLineSegment(sketch, "E15.1.1.10", {"start": v(12.48, 52.78) * mm, "end": v(18.56, 52.78) * mm});
            skLineSegment(sketch, "E15.1.1.11", {"start": v(12.48, 57.49) * mm, "end": v(18.56, 57.49) * mm});
            skLineSegment(sketch, "E15.1.1.12", {"start": v(12.48, 61.04) * mm, "end": v(18.56, 61.04) * mm});
            skLineSegment(sketch, "E15.1.1.13", {"start": v(12.48, 64.6) * mm, "end": v(18.56, 64.6) * mm});
            skLineSegment(sketch, "E15.1.1.14", {"start": v(12.48, 58.12) * mm, "end": v(18.56, 58.12) * mm});
            skLineSegment(sketch, "E15.1.1.15", {"start": v(5.08, 66.32) * mm, "end": v(18.55, 66.32) * mm});
            skLineSegment(sketch, "E15.1.1.16", {"start": v(5.08, 49.3) * mm, "end": v(18.55, 49.3) * mm});
            skLineSegment(sketch, "E15.1.1.17", {"start": v(5.08, 66.32) * mm, "end": v(5.08, 49.3) * mm});
            skLineSegment(sketch, "E15.1.1.18", {"start": v(12.48, 53.93) * mm, "end": v(18.56, 53.93) * mm});
            skLineSegment(sketch, "E15.1.1.19", {"start": v(6.35, 57.82) * mm, "end": v(6.35, 60.36) * mm});
            skLineSegment(sketch, "E15.1.1.20", {"start": v(6.35, 55.28) * mm, "end": v(5.08, 55.28) * mm});
            skLineSegment(sketch, "E15.1.1.21", {"start": v(6.35, 60.36) * mm, "end": v(5.08, 60.36) * mm});
            skLineSegment(sketch, "E15.1.1.22", {"start": v(6.35, 57.82) * mm, "end": v(6.35, 55.28) * mm});
            skLineSegment(sketch, "E15.1.1.23", {"start": v(12.48, 64.6) * mm, "end": v(12.48, 63.45) * mm});
            skLineSegment(sketch, "E15.1.1.24", {"start": v(18.55, 66.32) * mm, "end": v(18.55, 49.3) * mm});
            skLineSegment(sketch, "E15.1.1.25", {"start": v(18.56, 64.6) * mm, "end": v(18.56, 63.45) * mm});
            skLineSegment(sketch, "E15.1.1.26", {"start": v(18.56, 62.82) * mm, "end": v(18.56, 61.67) * mm});
            skLineSegment(sketch, "E15.1.1.27", {"start": v(12.48, 52.15) * mm, "end": v(12.48, 51) * mm});
            skLineSegment(sketch, "E15.1.1.28", {"start": v(18.56, 61.04) * mm, "end": v(18.56, 59.9) * mm});
            skLineSegment(sketch, "E15.1.1.29", {"start": v(12.48, 53.93) * mm, "end": v(12.48, 52.78) * mm});
            skLineSegment(sketch, "E15.1.1.30", {"start": v(18.56, 55.7) * mm, "end": v(18.56, 54.56) * mm});
            skLineSegment(sketch, "E15.1.1.31", {"start": v(12.48, 51) * mm, "end": v(12.48, 52.78) * mm, "construction": true});
            skLineSegment(sketch, "E15.1.1.32", {"start": v(12.48, 62.82) * mm, "end": v(12.48, 61.67) * mm});
            skLineSegment(sketch, "E15.1.1.33", {"start": v(18.56, 52.15) * mm, "end": v(18.56, 51) * mm});
            skLineSegment(sketch, "E15.1.1.34", {"start": v(18.56, 53.93) * mm, "end": v(18.56, 52.78) * mm});
            skLineSegment(sketch, "E15.1.1.35", {"start": v(12.48, 61.04) * mm, "end": v(12.48, 59.9) * mm});
            skLineSegment(sketch, "E15.1.1.36", {"start": v(18.56, 57.49) * mm, "end": v(18.56, 58.12) * mm});
            skLineSegment(sketch, "E15.1.1.37", {"start": v(12.48, 55.7) * mm, "end": v(12.48, 54.56) * mm});
            skLineSegment(sketch, "E15.1.1.38", {"start": v(18.56, 57.49) * mm, "end": v(18.56, 56.34) * mm});
            skLineSegment(sketch, "E15.1.1.39", {"start": v(18.56, 59.26) * mm, "end": v(18.56, 58.12) * mm});
            skLineSegment(sketch, "E15.1.1.40", {"start": v(12.48, 59.26) * mm, "end": v(12.48, 58.12) * mm});
            skLineSegment(sketch, "E15.1.1.41", {"start": v(12.48, 57.49) * mm, "end": v(12.48, 56.34) * mm});
            skLineSegment(sketch, "E15.1.2.0", {"start": v(12.48, 33.48) * mm, "end": v(18.56, 33.48) * mm});
            skLineSegment(sketch, "E15.1.2.1", {"start": v(12.48, 31.07) * mm, "end": v(18.56, 31.07) * mm});
            skLineSegment(sketch, "E15.1.2.2", {"start": v(12.48, 41.74) * mm, "end": v(18.56, 41.74) * mm});
            skLineSegment(sketch, "E15.1.2.3", {"start": v(12.48, 42.37) * mm, "end": v(18.56, 42.37) * mm});
            skLineSegment(sketch, "E15.1.2.4", {"start": v(12.48, 35.26) * mm, "end": v(18.56, 35.26) * mm});
            skLineSegment(sketch, "E15.1.2.5", {"start": v(12.48, 38.81) * mm, "end": v(18.56, 38.81) * mm});
            skLineSegment(sketch, "E15.1.2.6", {"start": v(12.48, 40.59) * mm, "end": v(18.56, 40.59) * mm});
            skLineSegment(sketch, "E15.1.2.7", {"start": v(12.48, 29.92) * mm, "end": v(18.56, 29.92) * mm});
            skLineSegment(sketch, "E15.1.2.8", {"start": v(12.48, 34.63) * mm, "end": v(18.56, 34.63) * mm});
            skLineSegment(sketch, "E15.1.2.9", {"start": v(12.48, 38.18) * mm, "end": v(18.56, 38.18) * mm});
            skLineSegment(sketch, "E15.1.2.10", {"start": v(12.48, 31.7) * mm, "end": v(18.56, 31.7) * mm});
            skLineSegment(sketch, "E15.1.2.11", {"start": v(12.48, 36.4) * mm, "end": v(18.56, 36.4) * mm});
            skLineSegment(sketch, "E15.1.2.12", {"start": v(12.48, 39.96) * mm, "end": v(18.56, 39.96) * mm});
            skLineSegment(sketch, "E15.1.2.13", {"start": v(12.48, 43.52) * mm, "end": v(18.56, 43.52) * mm});
            skLineSegment(sketch, "E15.1.2.14", {"start": v(12.48, 37.03) * mm, "end": v(18.56, 37.03) * mm});
            skLineSegment(sketch, "E15.1.2.15", {"start": v(5.08, 45.24) * mm, "end": v(18.55, 45.24) * mm});
            skLineSegment(sketch, "E15.1.2.16", {"start": v(5.08, 28.23) * mm, "end": v(18.55, 28.23) * mm});
            skLineSegment(sketch, "E15.1.2.17", {"start": v(5.08, 45.24) * mm, "end": v(5.08, 28.23) * mm});
            skLineSegment(sketch, "E15.1.2.18", {"start": v(12.48, 32.85) * mm, "end": v(18.56, 32.85) * mm});
            skLineSegment(sketch, "E15.1.2.19", {"start": v(6.35, 36.73) * mm, "end": v(6.35, 39.27) * mm});
            skLineSegment(sketch, "E15.1.2.20", {"start": v(6.35, 34.2) * mm, "end": v(5.08, 34.2) * mm});
            skLineSegment(sketch, "E15.1.2.21", {"start": v(6.35, 39.27) * mm, "end": v(5.08, 39.27) * mm});
            skLineSegment(sketch, "E15.1.2.22", {"start": v(6.35, 36.73) * mm, "end": v(6.35, 34.2) * mm});
            skLineSegment(sketch, "E15.1.2.23", {"start": v(12.48, 43.52) * mm, "end": v(12.48, 42.37) * mm});
            skLineSegment(sketch, "E15.1.2.24", {"start": v(18.55, 45.24) * mm, "end": v(18.55, 28.23) * mm});
            skLineSegment(sketch, "E15.1.2.25", {"start": v(18.56, 43.52) * mm, "end": v(18.56, 42.37) * mm});
            skLineSegment(sketch, "E15.1.2.26", {"start": v(18.56, 41.74) * mm, "end": v(18.56, 40.59) * mm});
            skLineSegment(sketch, "E15.1.2.27", {"start": v(12.48, 31.07) * mm, "end": v(12.48, 29.92) * mm});
            skLineSegment(sketch, "E15.1.2.28", {"start": v(18.56, 39.96) * mm, "end": v(18.56, 38.81) * mm});
            skLineSegment(sketch, "E15.1.2.29", {"start": v(12.48, 32.85) * mm, "end": v(12.48, 31.7) * mm});
            skLineSegment(sketch, "E15.1.2.30", {"start": v(18.56, 34.63) * mm, "end": v(18.56, 33.48) * mm});
            skLineSegment(sketch, "E15.1.2.31", {"start": v(12.48, 29.92) * mm, "end": v(12.48, 31.7) * mm, "construction": true});
            skLineSegment(sketch, "E15.1.2.32", {"start": v(12.48, 41.74) * mm, "end": v(12.48, 40.59) * mm});
            skLineSegment(sketch, "E15.1.2.33", {"start": v(18.56, 31.07) * mm, "end": v(18.56, 29.92) * mm});
            skLineSegment(sketch, "E15.1.2.34", {"start": v(18.56, 32.85) * mm, "end": v(18.56, 31.7) * mm});
            skLineSegment(sketch, "E15.1.2.35", {"start": v(12.48, 39.96) * mm, "end": v(12.48, 38.81) * mm});
            skLineSegment(sketch, "E15.1.2.36", {"start": v(18.56, 36.4) * mm, "end": v(18.56, 37.03) * mm});
            skLineSegment(sketch, "E15.1.2.37", {"start": v(12.48, 34.63) * mm, "end": v(12.48, 33.48) * mm});
            skLineSegment(sketch, "E15.1.2.38", {"start": v(18.56, 36.4) * mm, "end": v(18.56, 35.26) * mm});
            skLineSegment(sketch, "E15.1.2.39", {"start": v(18.56, 38.18) * mm, "end": v(18.56, 37.03) * mm});
            skLineSegment(sketch, "E15.1.2.40", {"start": v(12.48, 38.18) * mm, "end": v(12.48, 37.03) * mm});
            skLineSegment(sketch, "E15.1.2.41", {"start": v(12.48, 36.4) * mm, "end": v(12.48, 35.26) * mm});
            skLineSegment(sketch, "E15.1.3.0", {"start": v(12.48, 12.4) * mm, "end": v(18.56, 12.4) * mm});
            skLineSegment(sketch, "E15.1.3.1", {"start": v(12.48, 9.99) * mm, "end": v(18.56, 9.99) * mm});
            skLineSegment(sketch, "E15.1.3.2", {"start": v(12.48, 20.66) * mm, "end": v(18.56, 20.66) * mm});
            skLineSegment(sketch, "E15.1.3.3", {"start": v(12.48, 21.29) * mm, "end": v(18.56, 21.29) * mm});
            skLineSegment(sketch, "E15.1.3.4", {"start": v(12.48, 14.17) * mm, "end": v(18.56, 14.17) * mm});
            skLineSegment(sketch, "E15.1.3.5", {"start": v(12.48, 17.73) * mm, "end": v(18.56, 17.73) * mm});
            skLineSegment(sketch, "E15.1.3.6", {"start": v(12.48, 19.5) * mm, "end": v(18.56, 19.5) * mm});
            skLineSegment(sketch, "E15.1.3.7", {"start": v(12.48, 8.84) * mm, "end": v(18.56, 8.84) * mm});
            skLineSegment(sketch, "E15.1.3.8", {"start": v(12.48, 13.54) * mm, "end": v(18.56, 13.54) * mm});
            skLineSegment(sketch, "E15.1.3.9", {"start": v(12.48, 17.1) * mm, "end": v(18.56, 17.1) * mm});
            skLineSegment(sketch, "E15.1.3.10", {"start": v(12.48, 10.62) * mm, "end": v(18.56, 10.62) * mm});
            skLineSegment(sketch, "E15.1.3.11", {"start": v(12.48, 15.32) * mm, "end": v(18.56, 15.32) * mm});
            skLineSegment(sketch, "E15.1.3.12", {"start": v(12.48, 18.88) * mm, "end": v(18.56, 18.88) * mm});
            skLineSegment(sketch, "E15.1.3.13", {"start": v(12.48, 22.43) * mm, "end": v(18.56, 22.43) * mm});
            skLineSegment(sketch, "E15.1.3.14", {"start": v(12.48, 15.95) * mm, "end": v(18.56, 15.95) * mm});
            skLineSegment(sketch, "E15.1.3.15", {"start": v(5.08, 24.16) * mm, "end": v(18.55, 24.16) * mm});
            skLineSegment(sketch, "E15.1.3.16", {"start": v(5.08, 7.14) * mm, "end": v(18.55, 7.14) * mm});
            skLineSegment(sketch, "E15.1.3.17", {"start": v(5.08, 24.16) * mm, "end": v(5.08, 7.14) * mm});
            skLineSegment(sketch, "E15.1.3.18", {"start": v(12.48, 11.77) * mm, "end": v(18.56, 11.77) * mm});
            skLineSegment(sketch, "E15.1.3.19", {"start": v(6.35, 15.65) * mm, "end": v(6.35, 18.2) * mm});
            skLineSegment(sketch, "E15.1.3.20", {"start": v(6.35, 13.11) * mm, "end": v(5.08, 13.11) * mm});
            skLineSegment(sketch, "E15.1.3.21", {"start": v(6.35, 18.2) * mm, "end": v(5.08, 18.2) * mm});
            skLineSegment(sketch, "E15.1.3.22", {"start": v(6.35, 15.65) * mm, "end": v(6.35, 13.11) * mm});
            skLineSegment(sketch, "E15.1.3.23", {"start": v(12.48, 22.43) * mm, "end": v(12.48, 21.29) * mm});
            skLineSegment(sketch, "E15.1.3.24", {"start": v(18.55, 24.16) * mm, "end": v(18.55, 7.14) * mm});
            skLineSegment(sketch, "E15.1.3.25", {"start": v(18.56, 22.43) * mm, "end": v(18.56, 21.29) * mm});
            skLineSegment(sketch, "E15.1.3.26", {"start": v(18.56, 20.66) * mm, "end": v(18.56, 19.5) * mm});
            skLineSegment(sketch, "E15.1.3.27", {"start": v(12.48, 9.99) * mm, "end": v(12.48, 8.84) * mm});
            skLineSegment(sketch, "E15.1.3.28", {"start": v(18.56, 18.88) * mm, "end": v(18.56, 17.73) * mm});
            skLineSegment(sketch, "E15.1.3.29", {"start": v(12.48, 11.77) * mm, "end": v(12.48, 10.62) * mm});
            skLineSegment(sketch, "E15.1.3.30", {"start": v(18.56, 13.54) * mm, "end": v(18.56, 12.4) * mm});
            skLineSegment(sketch, "E15.1.3.31", {"start": v(12.48, 8.84) * mm, "end": v(12.48, 10.62) * mm, "construction": true});
            skLineSegment(sketch, "E15.1.3.32", {"start": v(12.48, 20.66) * mm, "end": v(12.48, 19.5) * mm});
            skLineSegment(sketch, "E15.1.3.33", {"start": v(18.56, 9.99) * mm, "end": v(18.56, 8.84) * mm});
            skLineSegment(sketch, "E15.1.3.34", {"start": v(18.56, 11.77) * mm, "end": v(18.56, 10.62) * mm});
            skLineSegment(sketch, "E15.1.3.35", {"start": v(12.48, 18.88) * mm, "end": v(12.48, 17.73) * mm});
            skLineSegment(sketch, "E15.1.3.36", {"start": v(18.56, 15.32) * mm, "end": v(18.56, 15.95) * mm});
            skLineSegment(sketch, "E15.1.3.37", {"start": v(12.48, 13.54) * mm, "end": v(12.48, 12.4) * mm});
            skLineSegment(sketch, "E15.1.3.38", {"start": v(18.56, 15.32) * mm, "end": v(18.56, 14.17) * mm});
            skLineSegment(sketch, "E15.1.3.39", {"start": v(18.56, 17.1) * mm, "end": v(18.56, 15.95) * mm});
            skLineSegment(sketch, "E15.1.3.40", {"start": v(12.48, 17.1) * mm, "end": v(12.48, 15.95) * mm});
            skLineSegment(sketch, "E15.1.3.41", {"start": v(12.48, 15.32) * mm, "end": v(12.48, 14.17) * mm});
            skLineSegment(sketch, "E15.direction1", {"start": v(5.08, 70.39) * mm, "end": v(5.08, 70.39) * mm});
            skLineSegment(sketch, "E16.MirrorCS", {"start": v(35.04, 13.54) * mm, "end": v(35.04, 12.4) * mm});
            skLineSegment(sketch, "E17.MirrorCS", {"start": v(35.04, 15.32) * mm, "end": v(35.04, 14.17) * mm});
            skLineSegment(sketch, "E18.MirrorCS", {"start": v(41.12, 12.4) * mm, "end": v(35.04, 12.4) * mm});
            skLineSegment(sketch, "E19.MirrorCS", {"start": v(35.04, 15.32) * mm, "end": v(35.04, 15.95) * mm});
            skLineSegment(sketch, "E20.MirrorCS", {"start": v(41.12, 13.54) * mm, "end": v(41.12, 12.4) * mm});
            skLineSegment(sketch, "E21.MirrorCS", {"start": v(41.12, 11.77) * mm, "end": v(35.04, 11.77) * mm});
            skLineSegment(sketch, "E22.MirrorCS", {"start": v(41.12, 37.03) * mm, "end": v(35.04, 37.03) * mm});
            skLineSegment(sketch, "E23.MirrorCS", {"start": v(41.12, 11.77) * mm, "end": v(41.12, 10.62) * mm});
            skLineSegment(sketch, "E24.MirrorCS", {"start": v(35.04, 59.26) * mm, "end": v(35.04, 58.12) * mm});
            skLineSegment(sketch, "E25.MirrorCS", {"start": v(41.12, 9.99) * mm, "end": v(41.12, 8.84) * mm});
            skLineSegment(sketch, "E26.MirrorCS", {"start": v(41.12, 14.17) * mm, "end": v(35.04, 14.17) * mm});
            skLineSegment(sketch, "E27.MirrorCS", {"start": v(35.04, 17.1) * mm, "end": v(35.04, 15.95) * mm});
            skLineSegment(sketch, "E28.MirrorCS", {"start": v(41.12, 57.49) * mm, "end": v(41.12, 56.34) * mm});
            skLineSegment(sketch, "E29.MirrorCS", {"start": v(41.12, 13.54) * mm, "end": v(35.04, 13.54) * mm});
            skLineSegment(sketch, "E30.MirrorCS", {"start": v(35.04, 36.4) * mm, "end": v(35.04, 37.03) * mm});
            skLineSegment(sketch, "E31.MirrorCS", {"start": v(41.12, 36.4) * mm, "end": v(35.04, 36.4) * mm});
            skLineSegment(sketch, "E32.MirrorCS", {"start": v(41.12, 15.32) * mm, "end": v(41.12, 14.17) * mm});
            skLineSegment(sketch, "E33.MirrorCS", {"start": v(41.12, 56.34) * mm, "end": v(35.04, 56.34) * mm});
            skLineSegment(sketch, "E34.MirrorCS", {"start": v(35.04, 57.49) * mm, "end": v(35.04, 58.12) * mm});
            skLineSegment(sketch, "E35.MirrorCS", {"start": v(41.12, 38.18) * mm, "end": v(41.12, 37.03) * mm});
            skLineSegment(sketch, "E36.MirrorCS", {"start": v(41.12, 75.01) * mm, "end": v(35.04, 75.01) * mm});
            skLineSegment(sketch, "E37.MirrorCS", {"start": v(41.12, 61.04) * mm, "end": v(41.12, 59.9) * mm});
            skLineSegment(sketch, "E38.MirrorCS", {"start": v(41.12, 55.7) * mm, "end": v(35.04, 55.7) * mm});
            skLineSegment(sketch, "E39.MirrorCS", {"start": v(41.12, 36.4) * mm, "end": v(41.12, 35.26) * mm});
            skLineSegment(sketch, "E40.MirrorCS", {"start": v(41.12, 54.56) * mm, "end": v(35.04, 54.56) * mm});
            skLineSegment(sketch, "E41.MirrorCS", {"start": v(41.12, 59.26) * mm, "end": v(41.12, 58.12) * mm});
            skLineSegment(sketch, "E42.MirrorCS", {"start": v(35.04, 36.4) * mm, "end": v(35.04, 35.26) * mm});
            skLineSegment(sketch, "E43.MirrorCS", {"start": v(35.04, 38.18) * mm, "end": v(35.04, 37.03) * mm});
            skLineSegment(sketch, "E44.MirrorCS", {"start": v(41.12, 15.32) * mm, "end": v(35.04, 15.32) * mm});
            skLineSegment(sketch, "E45.MirrorCS", {"start": v(41.12, 57.49) * mm, "end": v(35.04, 57.49) * mm});
            skLineSegment(sketch, "E46.MirrorCS", {"start": v(41.12, 38.81) * mm, "end": v(35.04, 38.81) * mm});
            skLineSegment(sketch, "E47.MirrorCS", {"start": v(41.12, 59.26) * mm, "end": v(35.04, 59.26) * mm});
            skLineSegment(sketch, "E48.MirrorCS", {"start": v(35.04, 39.96) * mm, "end": v(35.04, 38.81) * mm});
            skLineSegment(sketch, "E49.MirrorCS", {"start": v(35.04, 57.49) * mm, "end": v(35.04, 56.34) * mm});
            skLineSegment(sketch, "E50.MirrorCS", {"start": v(41.12, 58.12) * mm, "end": v(35.04, 58.12) * mm});
            skLineSegment(sketch, "E51.MirrorCS", {"start": v(35.04, 55.7) * mm, "end": v(35.04, 54.56) * mm});
            skLineSegment(sketch, "E52.MirrorCS", {"start": v(41.12, 35.26) * mm, "end": v(35.04, 35.26) * mm});
            skLineSegment(sketch, "E53.MirrorCS", {"start": v(41.12, 59.9) * mm, "end": v(35.04, 59.9) * mm});
            skLineSegment(sketch, "E54.MirrorCS", {"start": v(41.12, 55.7) * mm, "end": v(41.12, 54.56) * mm});
            skLineSegment(sketch, "E55.MirrorCS", {"start": v(35.04, 76.79) * mm, "end": v(35.04, 75.64) * mm});
            skLineSegment(sketch, "E56.MirrorCS", {"start": v(41.12, 39.96) * mm, "end": v(41.12, 38.81) * mm});
            skLineSegment(sketch, "E57.MirrorCS", {"start": v(35.04, 80.35) * mm, "end": v(35.04, 79.2) * mm});
            skLineSegment(sketch, "E58.MirrorCS", {"start": v(41.12, 15.95) * mm, "end": v(35.04, 15.95) * mm});
            skLineSegment(sketch, "E59.MirrorCS", {"start": v(41.12, 34.63) * mm, "end": v(35.04, 34.63) * mm});
            skLineSegment(sketch, "E60.MirrorCS", {"start": v(35.04, 78.57) * mm, "end": v(35.04, 79.2) * mm});
            skLineSegment(sketch, "E61.MirrorCS", {"start": v(41.12, 77.42) * mm, "end": v(35.04, 77.42) * mm});
            skLineSegment(sketch, "E62.MirrorCS", {"start": v(35.04, 62.82) * mm, "end": v(35.04, 61.67) * mm});
            skLineSegment(sketch, "E63.MirrorCS", {"start": v(41.12, 18.88) * mm, "end": v(41.12, 17.73) * mm});
            skLineSegment(sketch, "E64.MirrorCS", {"start": v(41.12, 38.18) * mm, "end": v(35.04, 38.18) * mm});
            skLineSegment(sketch, "E65.MirrorCS", {"start": v(41.12, 8.84) * mm, "end": v(41.12, 10.62) * mm, "construction": true});
            skLineSegment(sketch, "E66.MirrorCS", {"start": v(35.04, 41.74) * mm, "end": v(35.04, 40.59) * mm});
            skLineSegment(sketch, "E67.MirrorCS", {"start": v(35.04, 34.63) * mm, "end": v(35.04, 33.48) * mm});
            skLineSegment(sketch, "E68.MirrorCS", {"start": v(41.12, 34.63) * mm, "end": v(41.12, 33.48) * mm});
            skLineSegment(sketch, "E69.MirrorCS", {"start": v(35.04, 18.88) * mm, "end": v(35.04, 17.73) * mm});
            skLineSegment(sketch, "E70.MirrorCS", {"start": v(41.12, 53.93) * mm, "end": v(35.04, 53.93) * mm});
            skLineSegment(sketch, "E71.MirrorCS", {"start": v(41.12, 52.15) * mm, "end": v(41.12, 51) * mm});
            skLineSegment(sketch, "E72.MirrorCS", {"start": v(35.04, 61.04) * mm, "end": v(35.04, 59.9) * mm});
            skLineSegment(sketch, "E73.MirrorCS", {"start": v(35.04, 64.6) * mm, "end": v(35.04, 63.45) * mm});
            skLineSegment(sketch, "E74.MirrorCS", {"start": v(41.12, 40.59) * mm, "end": v(35.04, 40.59) * mm});
            skLineSegment(sketch, "E75.MirrorCS", {"start": v(35.04, 78.57) * mm, "end": v(35.04, 77.42) * mm});
            skLineSegment(sketch, "E76.MirrorCS", {"start": v(41.12, 73.23) * mm, "end": v(41.12, 72.09) * mm});
            skLineSegment(sketch, "E77.MirrorCS", {"start": v(41.12, 78.57) * mm, "end": v(35.04, 78.57) * mm});
            skLineSegment(sketch, "E78.MirrorCS", {"start": v(41.12, 75.64) * mm, "end": v(35.04, 75.64) * mm});
            skLineSegment(sketch, "E79.MirrorCS", {"start": v(35.04, 11.77) * mm, "end": v(35.04, 10.62) * mm});
            skLineSegment(sketch, "E80.MirrorCS", {"start": v(41.12, 76.79) * mm, "end": v(35.04, 76.79) * mm});
            skLineSegment(sketch, "E81.MirrorCS", {"start": v(41.12, 39.96) * mm, "end": v(35.04, 39.96) * mm});
            skLineSegment(sketch, "E82.MirrorCS", {"start": v(41.12, 10.62) * mm, "end": v(35.04, 10.62) * mm});
            skLineSegment(sketch, "E83.MirrorCS", {"start": v(41.12, 9.99) * mm, "end": v(35.04, 9.99) * mm});
            skLineSegment(sketch, "E84.MirrorCS", {"start": v(41.12, 53.93) * mm, "end": v(41.12, 52.78) * mm});
            skLineSegment(sketch, "E85.MirrorCS", {"start": v(41.12, 73.86) * mm, "end": v(35.04, 73.86) * mm});
            skLineSegment(sketch, "E86.MirrorCS", {"start": v(41.12, 33.48) * mm, "end": v(35.04, 33.48) * mm});
            skLineSegment(sketch, "E87.MirrorCS", {"start": v(41.12, 52.78) * mm, "end": v(35.04, 52.78) * mm});
            skLineSegment(sketch, "E88.MirrorCS", {"start": v(41.12, 41.74) * mm, "end": v(41.12, 40.59) * mm});
            skLineSegment(sketch, "E89.MirrorCS", {"start": v(41.12, 82.12) * mm, "end": v(41.12, 80.98) * mm});
            skLineSegment(sketch, "E90.MirrorCS", {"start": v(41.12, 80.35) * mm, "end": v(35.04, 80.35) * mm});
            skLineSegment(sketch, "E91.MirrorCS", {"start": v(41.12, 76.79) * mm, "end": v(41.12, 75.64) * mm});
            skLineSegment(sketch, "E92.MirrorCS", {"start": v(41.12, 62.82) * mm, "end": v(35.04, 62.82) * mm});
            skLineSegment(sketch, "E93.MirrorCS", {"start": v(35.04, 82.12) * mm, "end": v(35.04, 80.98) * mm});
            skLineSegment(sketch, "E94.MirrorCS", {"start": v(41.12, 62.82) * mm, "end": v(41.12, 61.67) * mm});
            skLineSegment(sketch, "E95.MirrorCS", {"start": v(41.12, 18.88) * mm, "end": v(35.04, 18.88) * mm});
            skLineSegment(sketch, "E96.MirrorCS", {"start": v(41.12, 75.01) * mm, "end": v(41.12, 73.86) * mm});
            skLineSegment(sketch, "E97.MirrorCS", {"start": v(35.04, 53.93) * mm, "end": v(35.04, 52.78) * mm});
            skLineSegment(sketch, "E98.MirrorCS", {"start": v(41.12, 17.73) * mm, "end": v(35.04, 17.73) * mm});
            skLineSegment(sketch, "E99.MirrorCS", {"start": v(35.04, 75.01) * mm, "end": v(35.04, 73.86) * mm});
            skLineSegment(sketch, "E100.MirrorCS", {"start": v(41.12, 61.04) * mm, "end": v(35.04, 61.04) * mm});
            skLineSegment(sketch, "E101.MirrorCS", {"start": v(41.12, 17.1) * mm, "end": v(41.12, 15.95) * mm});
            skLineSegment(sketch, "E102.MirrorCS", {"start": v(35.04, 85.68) * mm, "end": v(35.04, 84.53) * mm});
            skLineSegment(sketch, "E103.MirrorCS", {"start": v(41.12, 78.57) * mm, "end": v(41.12, 77.42) * mm});
            skLineSegment(sketch, "E104.MirrorCS", {"start": v(41.12, 80.35) * mm, "end": v(41.12, 79.2) * mm});
            skLineSegment(sketch, "E105.MirrorCS", {"start": v(41.12, 61.67) * mm, "end": v(35.04, 61.67) * mm});
            skLineSegment(sketch, "E106.MirrorCS", {"start": v(35.04, 20.66) * mm, "end": v(35.04, 19.5) * mm});
            skLineSegment(sketch, "E107.MirrorCS", {"start": v(35.04, 83.9) * mm, "end": v(35.04, 82.75) * mm});
            skLineSegment(sketch, "E108.MirrorCS", {"start": v(41.12, 17.1) * mm, "end": v(35.04, 17.1) * mm});
            skLineSegment(sketch, "E109.MirrorCS", {"start": v(41.12, 42.37) * mm, "end": v(35.04, 42.37) * mm});
            skLineSegment(sketch, "E110.MirrorCS", {"start": v(41.12, 19.5) * mm, "end": v(35.04, 19.5) * mm});
            skLineSegment(sketch, "E111.MirrorCS", {"start": v(35.04, 73.23) * mm, "end": v(35.04, 72.09) * mm});
            skLineSegment(sketch, "E112.MirrorCS", {"start": v(41.12, 63.45) * mm, "end": v(35.04, 63.45) * mm});
            skLineSegment(sketch, "E113.MirrorCS", {"start": v(35.04, 43.52) * mm, "end": v(35.04, 42.37) * mm});
            skLineSegment(sketch, "E114.MirrorCS", {"start": v(41.12, 80.98) * mm, "end": v(35.04, 80.98) * mm});
            skLineSegment(sketch, "E115.MirrorCS", {"start": v(41.12, 79.2) * mm, "end": v(35.04, 79.2) * mm});
            skLineSegment(sketch, "E116.MirrorCS", {"start": v(41.12, 43.52) * mm, "end": v(35.04, 43.52) * mm});
            skLineSegment(sketch, "E117.MirrorCS", {"start": v(41.12, 41.74) * mm, "end": v(35.04, 41.74) * mm});
            skLineSegment(sketch, "E118.MirrorCS", {"start": v(41.12, 32.85) * mm, "end": v(35.04, 32.85) * mm});
            skLineSegment(sketch, "E119.MirrorCS", {"start": v(41.12, 73.23) * mm, "end": v(35.04, 73.23) * mm});
            skLineSegment(sketch, "E120.MirrorCS", {"start": v(41.12, 51) * mm, "end": v(41.12, 52.78) * mm, "construction": true});
            skLineSegment(sketch, "E121.MirrorCS", {"start": v(41.12, 43.52) * mm, "end": v(41.12, 42.37) * mm});
            skLineSegment(sketch, "E122.MirrorCS", {"start": v(41.12, 64.6) * mm, "end": v(41.12, 63.45) * mm});
            skLineSegment(sketch, "E123.MirrorCS", {"start": v(41.12, 32.85) * mm, "end": v(41.12, 31.7) * mm});
            skLineSegment(sketch, "E124.MirrorCS", {"start": v(35.04, 32.85) * mm, "end": v(35.04, 31.7) * mm});
            skLineSegment(sketch, "E125.MirrorCS", {"start": v(41.12, 72.09) * mm, "end": v(41.12, 73.86) * mm, "construction": true});
            skLineSegment(sketch, "E126.MirrorCS", {"start": v(41.12, 83.9) * mm, "end": v(41.12, 82.75) * mm});
            skLineSegment(sketch, "E127.MirrorCS", {"start": v(41.12, 72.09) * mm, "end": v(35.04, 72.09) * mm});
            skLineSegment(sketch, "E128.MirrorCS", {"start": v(41.12, 83.9) * mm, "end": v(35.04, 83.9) * mm});
            skLineSegment(sketch, "E129.MirrorCS", {"start": v(41.12, 82.12) * mm, "end": v(35.04, 82.12) * mm});
            skLineSegment(sketch, "E130.MirrorCS", {"start": v(41.12, 52.15) * mm, "end": v(35.04, 52.15) * mm});
            skLineSegment(sketch, "E131.MirrorCS", {"start": v(41.12, 31.7) * mm, "end": v(35.04, 31.7) * mm});
            skLineSegment(sketch, "E132.MirrorCS", {"start": v(41.12, 82.75) * mm, "end": v(35.04, 82.75) * mm});
            skLineSegment(sketch, "E133.MirrorCS", {"start": v(41.12, 20.66) * mm, "end": v(41.12, 19.5) * mm});
            skLineSegment(sketch, "E134.MirrorCS", {"start": v(41.12, 20.66) * mm, "end": v(35.04, 20.66) * mm});
            skLineSegment(sketch, "E135.MirrorCS", {"start": v(41.12, 31.07) * mm, "end": v(41.12, 29.92) * mm});
            skLineSegment(sketch, "E136.MirrorCS", {"start": v(41.12, 64.6) * mm, "end": v(35.04, 64.6) * mm});
            skLineSegment(sketch, "E137.MirrorCS", {"start": v(35.04, 9.99) * mm, "end": v(35.04, 8.84) * mm});
            skLineSegment(sketch, "E138.MirrorCS", {"start": v(41.12, 21.29) * mm, "end": v(35.04, 21.29) * mm});
            skLineSegment(sketch, "E139.MirrorCS", {"start": v(41.12, 8.84) * mm, "end": v(35.04, 8.84) * mm});
            skLineSegment(sketch, "E140.MirrorCS", {"start": v(41.12, 29.92) * mm, "end": v(41.12, 31.7) * mm, "construction": true});
            skLineSegment(sketch, "E141.MirrorCS", {"start": v(41.12, 85.68) * mm, "end": v(41.12, 84.53) * mm});
            skLineSegment(sketch, "E142.MirrorCS", {"start": v(41.12, 51) * mm, "end": v(35.04, 51) * mm});
            skLineSegment(sketch, "E143.MirrorCS", {"start": v(35.04, 52.15) * mm, "end": v(35.04, 51) * mm});
            skLineSegment(sketch, "E144.MirrorCS", {"start": v(35.04, 87.4) * mm, "end": v(35.04, 70.39) * mm});
            skLineSegment(sketch, "E145.MirrorCS", {"start": v(47.24, 57.82) * mm, "end": v(47.24, 55.28) * mm});
            skLineSegment(sketch, "E146.MirrorCS", {"start": v(35.04, 22.43) * mm, "end": v(35.04, 21.29) * mm});
            skLineSegment(sketch, "E147.MirrorCS", {"start": v(47.24, 15.65) * mm, "end": v(47.24, 13.11) * mm});
            skLineSegment(sketch, "E148.MirrorCS", {"start": v(41.12, 84.53) * mm, "end": v(35.04, 84.53) * mm});
            skLineSegment(sketch, "E149.MirrorCS", {"start": v(35.04, 31.07) * mm, "end": v(35.04, 29.92) * mm});
            skLineSegment(sketch, "E150.MirrorCS", {"start": v(35.04, 24.16) * mm, "end": v(35.04, 7.14) * mm});
            skLineSegment(sketch, "E151.MirrorCS", {"start": v(41.12, 22.43) * mm, "end": v(35.04, 22.43) * mm});
            skLineSegment(sketch, "E152.MirrorCS", {"start": v(41.12, 31.07) * mm, "end": v(35.04, 31.07) * mm});
            skLineSegment(sketch, "E153.MirrorCS", {"start": v(41.12, 29.92) * mm, "end": v(35.04, 29.92) * mm});
            skLineSegment(sketch, "E154.MirrorCS", {"start": v(41.12, 22.43) * mm, "end": v(41.12, 21.29) * mm});
            skLineSegment(sketch, "E155.MirrorCS", {"start": v(47.24, 15.65) * mm, "end": v(47.24, 18.2) * mm});
            skLineSegment(sketch, "E156.MirrorCS", {"start": v(41.12, 85.68) * mm, "end": v(35.04, 85.68) * mm});
            skLineSegment(sketch, "E157.MirrorCS", {"start": v(47.24, 76.36) * mm, "end": v(48.51, 76.36) * mm});
            skLineSegment(sketch, "E158.MirrorCS", {"start": v(47.24, 57.82) * mm, "end": v(47.24, 60.36) * mm});
            skLineSegment(sketch, "E159.MirrorCS", {"start": v(47.24, 78.9) * mm, "end": v(47.24, 81.44) * mm});
            skLineSegment(sketch, "E160.MirrorCS", {"start": v(47.24, 78.9) * mm, "end": v(47.24, 76.36) * mm});
            skLineSegment(sketch, "E161.MirrorCS", {"start": v(47.24, 13.11) * mm, "end": v(48.51, 13.11) * mm});
            skLineSegment(sketch, "E162.MirrorCS", {"start": v(47.24, 18.2) * mm, "end": v(48.51, 18.2) * mm});
            skLineSegment(sketch, "E163.MirrorCS", {"start": v(47.24, 34.2) * mm, "end": v(48.51, 34.2) * mm});
            skLineSegment(sketch, "E164.MirrorCS", {"start": v(48.51, 24.16) * mm, "end": v(48.51, 7.14) * mm});
            skLineSegment(sketch, "E165.MirrorCS", {"start": v(47.24, 60.36) * mm, "end": v(48.51, 60.36) * mm});
            skLineSegment(sketch, "E166.MirrorCS", {"start": v(47.24, 36.73) * mm, "end": v(47.24, 39.27) * mm});
            skLineSegment(sketch, "E167.MirrorCS", {"start": v(47.24, 55.28) * mm, "end": v(48.51, 55.28) * mm});
            skLineSegment(sketch, "E168.MirrorCS", {"start": v(35.04, 45.24) * mm, "end": v(35.04, 28.23) * mm});
            skLineSegment(sketch, "E169.MirrorCS", {"start": v(47.24, 81.44) * mm, "end": v(48.51, 81.44) * mm});
            skLineSegment(sketch, "E170.MirrorCS", {"start": v(47.24, 39.27) * mm, "end": v(48.51, 39.27) * mm});
            skLineSegment(sketch, "E171.MirrorCS", {"start": v(35.04, 66.32) * mm, "end": v(35.04, 49.3) * mm});
            skLineSegment(sketch, "E172.MirrorCS", {"start": v(47.24, 36.73) * mm, "end": v(47.24, 34.2) * mm});
            skLineSegment(sketch, "E173.MirrorCS", {"start": v(48.51, 45.24) * mm, "end": v(48.51, 28.23) * mm});
            skLineSegment(sketch, "E174.MirrorCS", {"start": v(48.51, 87.4) * mm, "end": v(35.04, 87.4) * mm});
            skLineSegment(sketch, "E175.MirrorCS", {"start": v(48.51, 66.32) * mm, "end": v(48.51, 49.3) * mm});
            skLineSegment(sketch, "E176.MirrorCS", {"start": v(48.51, 70.39) * mm, "end": v(35.04, 70.39) * mm});
            skLineSegment(sketch, "E177.MirrorCS", {"start": v(48.51, 28.23) * mm, "end": v(35.04, 28.23) * mm});
            skLineSegment(sketch, "E178.MirrorCS", {"start": v(48.51, 87.4) * mm, "end": v(48.51, 70.39) * mm});
            skLineSegment(sketch, "E179.MirrorCS", {"start": v(48.51, 24.16) * mm, "end": v(35.04, 24.16) * mm});
            skLineSegment(sketch, "E180.MirrorCS", {"start": v(48.51, 49.3) * mm, "end": v(35.04, 49.3) * mm});
            skLineSegment(sketch, "E181.MirrorCS", {"start": v(48.51, 45.24) * mm, "end": v(35.04, 45.24) * mm});
            skLineSegment(sketch, "E182.MirrorCS", {"start": v(48.51, 7.14) * mm, "end": v(35.04, 7.14) * mm});
            skLineSegment(sketch, "E183.MirrorCS", {"start": v(48.51, 66.32) * mm, "end": v(35.04, 66.32) * mm});
            skSolve(sketch);
        }
        {
            var Q0;
            {var subQ3=sQuery(id+"F5.wireOp",EDGE,"E15.1.0.15");Q0=makeQuery(id+"F5.imprint","IMPRINT",FACE,{"disambiguationData":[TD([[makeQuery(id+"F5.imprint","IMPRINT",EDGE,{"derivedFrom":subQ3}),-1.0]])]});}
            var Q1;
            {var subQ8=sQuery(id+"F5.wireOp",EDGE,"E76.MirrorCS");Q1=makeQuery(id+"F5.imprint","IMPRINT",FACE,{"disambiguationData":[TD([[makeQuery(id+"F5.imprint","IMPRINT",EDGE,{"derivedFrom":subQ8}),1.0]])]});}
            var Q2;
            {var subQ13=sQuery(id+"F5.wireOp",EDGE,"E37.MirrorCS");Q2=makeQuery(id+"F5.imprint","IMPRINT",FACE,{"disambiguationData":[TD([[makeQuery(id+"F5.imprint","IMPRINT",EDGE,{"derivedFrom":subQ13}),1.0]])]});}
            var Q3;
            {var subQ3=sQuery(id+"F5.wireOp",EDGE,"E15.1.1.15");Q3=makeQuery(id+"F5.imprint","IMPRINT",FACE,{"disambiguationData":[TD([[makeQuery(id+"F5.imprint","IMPRINT",EDGE,{"derivedFrom":subQ3}),-1.0]])]});}
            var Q4;
            {var subQ10=sQuery(id+"F5.wireOp",EDGE,"E39.MirrorCS");Q4=makeQuery(id+"F5.imprint","IMPRINT",FACE,{"disambiguationData":[TD([[makeQuery(id+"F5.imprint","IMPRINT",EDGE,{"derivedFrom":subQ10}),1.0]])]});}
            var Q5;
            {var subQ3=sQuery(id+"F5.wireOp",EDGE,"E15.1.2.15");Q5=makeQuery(id+"F5.imprint","IMPRINT",FACE,{"disambiguationData":[TD([[makeQuery(id+"F5.imprint","IMPRINT",EDGE,{"derivedFrom":subQ3}),-1.0]])]});}
            var Q6;
            {var subQ21=sQuery(id+"F5.wireOp",EDGE,"E20.MirrorCS");Q6=makeQuery(id+"F5.imprint","IMPRINT",FACE,{"disambiguationData":[TD([[makeQuery(id+"F5.imprint","IMPRINT",EDGE,{"derivedFrom":subQ21}),1.0]])]});}
            var Q7;
            {var subQ3=sQuery(id+"F5.wireOp",EDGE,"E15.1.3.15");Q7=makeQuery(id+"F5.imprint","IMPRINT",FACE,{"disambiguationData":[TD([[makeQuery(id+"F5.imprint","IMPRINT",EDGE,{"derivedFrom":subQ3}),-1.0]])]});}
            extrude(context, id + "F6", {"entities" : qUnion([Q0, Q1, Q2, Q3, Q4, Q5, Q6, Q7]), "operationType" : NewBodyOperationType.REMOVE, "oppositeDirection" : true, "depth" : 25.4 * mm, "offsetDistance" : 25.4 * mm});
        }
    });
